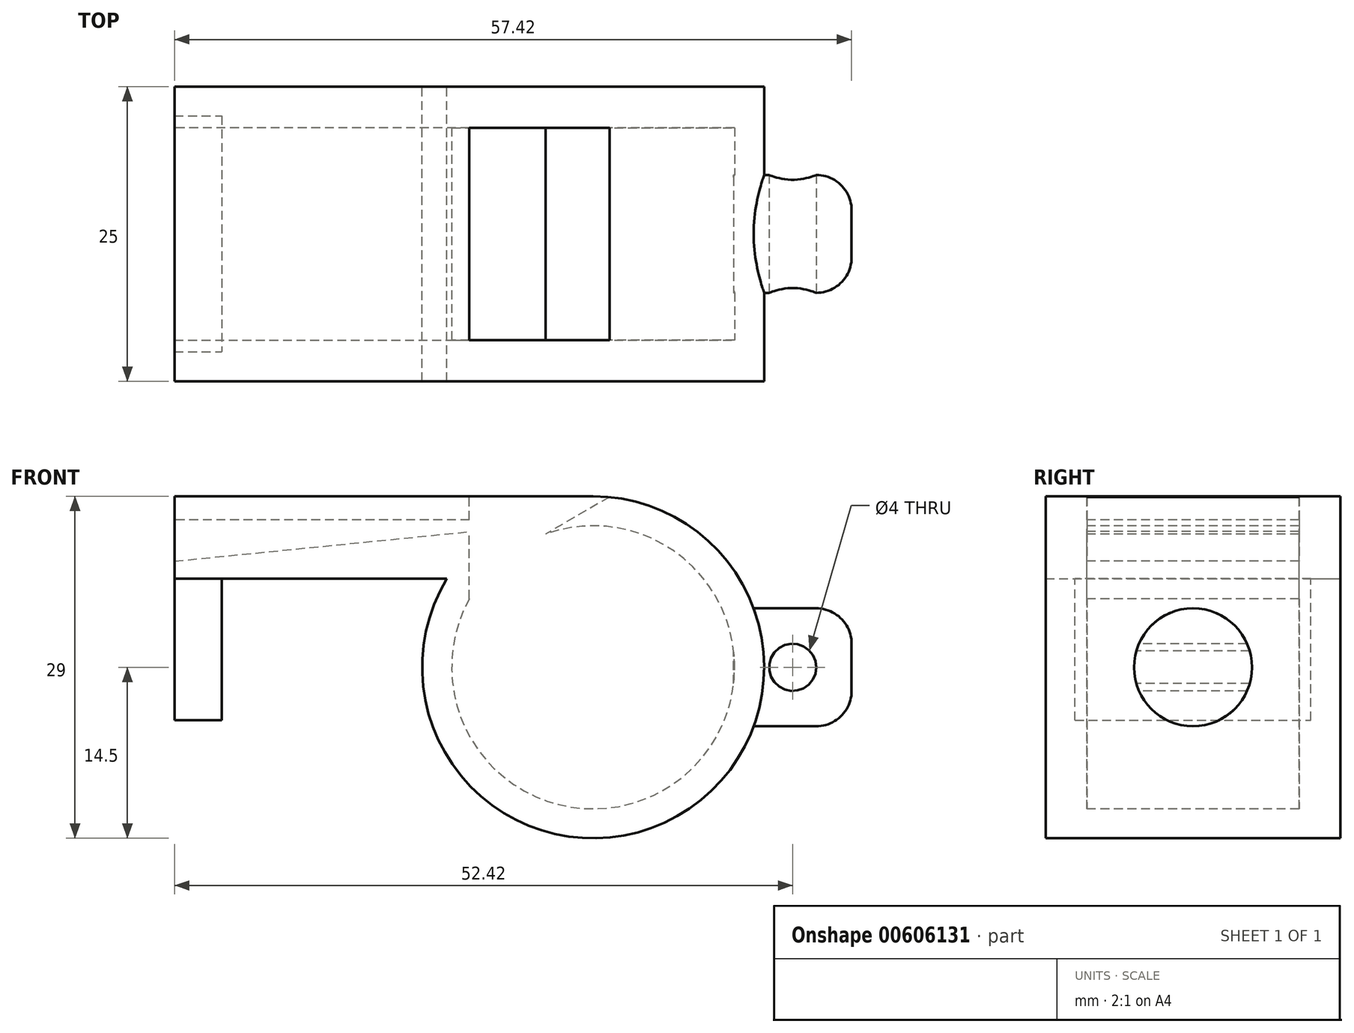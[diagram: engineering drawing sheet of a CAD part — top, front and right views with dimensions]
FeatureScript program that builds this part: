
annotation { "Feature Type Name" : "Feature", "Feature Type Description" : "" }
export const myFeature = defineFeature(function(context is Context, id is Id, definition is map)
    precondition{}
    {
        {
            var Q0;
            Q0=qCreatedBy(makeId("Front.planeOp"),FACE);
            var sketch = newSketch(context, id + "F0", { "sketchPlane" : qUnion([Q0])});
            skArc(sketch, "E0", {"start": v(-12.4, 7.5) * mm, "mid": v(7.12, -12.63) * mm, "end": v(0, 14.5) * mm});
            skLineSegment(sketch, "E1", {"start": v(0, 14.5) * mm, "end": v(-35.5, 14.5) * mm});
            skLineSegment(sketch, "E2", {"start": v(-35.5, 14.5) * mm, "end": v(-35.5, 7.5) * mm});
            skLineSegment(sketch, "E3", {"start": v(-35.5, 7.5) * mm, "end": v(-12.4, 7.5) * mm});
            skSolve(sketch);
        }
        {
            var Q0;
            Q0 = qSketchRegion(id + "F0", true);
            extrude(context, id + "F1", {"entities" : qUnion([Q0]), "depth" : 25 * mm, "offsetDistance" : 25 * mm, "symmetric" : true});
        }
        {
            var Q0;
            Q0=qCreatedBy(makeId("Front.planeOp"),FACE);
            var sketch = newSketch(context, id + "F2", { "sketchPlane" : qUnion([Q0])});
            skArc(sketch, "E4", {"start": v(-10.5, 5.8) * mm, "mid": v(7.77, -9.14) * mm, "end": v(-4.05, 11.3) * mm});
            skLineSegment(sketch, "E5", {"start": v(-10.5, 12.5) * mm, "end": v(-35.5, 12.5) * mm});
            skLineSegment(sketch, "E6", {"start": v(-35.5, 12.5) * mm, "end": v(-35.5, 9) * mm});
            skLineSegment(sketch, "E7", {"start": v(-10.5, 12.5) * mm, "end": v(-10.5, 14.5) * mm});
            skLineSegment(sketch, "E8", {"start": v(-10.5, 14.5) * mm, "end": v(1.5, 14.5) * mm});
            skLineSegment(sketch, "E9", {"start": v(1.5, 14.5) * mm, "end": v(-4.05, 11.3) * mm});
            skLineSegment(sketch, "E10", {"start": v(-35.5, 9) * mm, "end": v(-10.5, 11.5) * mm});
            skLineSegment(sketch, "E11", {"start": v(-10.5, 5.8) * mm, "end": v(-10.5, 11.5) * mm});
            skSolve(sketch);
        }
        {
            var Q0;
            Q0 = qSketchRegion(id + "F2", true);
            extrude(context, id + "F3", {"entities" : qUnion([Q0]), "operationType" : NewBodyOperationType.REMOVE, "oppositeDirection" : true, "depth" : 18 * mm, "offsetDistance" : 25 * mm, "symmetric" : true});
        }
        {
            var Q0;
            Q0=qCreatedBy(makeId("Front.planeOp"),FACE);
            var sketch = newSketch(context, id + "F4", { "sketchPlane" : qUnion([Q0])});
            skLineSegment(sketch, "E12.bottom", {"start": v(11.92, 5) * mm, "end": v(21.92, 5) * mm});
            skLineSegment(sketch, "E12.top", {"start": v(11.92, 0) * mm, "end": v(21.92, 0) * mm});
            skLineSegment(sketch, "E12.left", {"start": v(11.92, 5) * mm, "end": v(11.92, 0) * mm});
            skLineSegment(sketch, "E12.right", {"start": v(21.92, 5) * mm, "end": v(21.92, 0) * mm});
            skSolve(sketch);
        }
        {
            var Q0;
            Q0 = qSketchRegion(id + "F4", true);
            var Q1;
            Q1=sQuery(id+"F4.wireOp",EDGE,"E12.top");
            revolve(context, id + "F5", {"operationType" : NewBodyOperationType.ADD, "entities" : qUnion([Q0]), "axis" : qUnion([Q1]), "revolveType" : RevolveType.FULL});
        }
        {
            var Q0;
            Q0=makeQuery(id+"F5.opRevolve","SWEPT_EDGE",EDGE,{"disambiguationData":[OSD([sQuery(id+"F4.wireOp",EDGE,"E12.bottom"),sQuery(id+"F4.wireOp",EDGE,"E12.right")])]});
            fillet(context, id + "F6", {"entities" : qUnion([Q0]), "radius" : 3 * mm, "tangentPropagation" : true, "allowEdgeOverflow" : false});
        }
        {
            var Q0;
            Q0=qCreatedBy(makeId("Front.planeOp"),FACE);
            var sketch = newSketch(context, id + "F7", { "sketchPlane" : qUnion([Q0])});
            skCircle(sketch, "E13", {"center": v(16.92, 0) * mm, "radius": 2 * mm});
            skSolve(sketch);
        }
        {
            var Q0;
            Q0 = qSketchRegion(id + "F7", true);
            extrude(context, id + "F8", {"entities" : qUnion([Q0]), "operationType" : NewBodyOperationType.REMOVE, "oppositeDirection" : true, "depth" : 10 * mm, "offsetDistance" : 25 * mm, "symmetric" : true});
        }
        {
            var Q0;
            Q0=makeQuery(id+"F1.opExtrude","SWEPT_FACE",FACE,{"disambiguationData":[OSD([sQuery(id+"F0.wireOp",EDGE,"E3")])]});
            var sketch = newSketch(context, id + "F9", { "sketchPlane" : qUnion([Q0])});
            skLineSegment(sketch, "E14.bottom", {"start": v(-35.5, -10) * mm, "end": v(-31.5, -10) * mm});
            skLineSegment(sketch, "E14.top", {"start": v(-35.5, 10) * mm, "end": v(-31.5, 10) * mm});
            skLineSegment(sketch, "E14.left", {"start": v(-35.5, -10) * mm, "end": v(-35.5, 10) * mm});
            skLineSegment(sketch, "E14.right", {"start": v(-31.5, -10) * mm, "end": v(-31.5, 10) * mm});
            skSolve(sketch);
        }
        {
            var Q0;
            Q0 = qSketchRegion(id + "F9", true);
            extrude(context, id + "F10", {"entities" : qUnion([Q0]), "operationType" : NewBodyOperationType.ADD, "depth" : 12 * mm, "offsetDistance" : 25 * mm});
        }
        {
            var Q0;
            Q0 = qSketchRegion(id + "F9", true);
            extrude(context, id + "F11", {"entities" : qUnion([Q0]), "operationType" : NewBodyOperationType.ADD, "depth" : 0.7 * mm, "offsetDistance" : 25 * mm});
        }
    });
